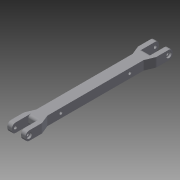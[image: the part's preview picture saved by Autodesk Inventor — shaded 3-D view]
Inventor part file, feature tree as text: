
AUTODESK INVENTOR PART (.ipt)
format: ipt  version: 2015 (Build 190159000, 159)  size: 180,736 bytes
history: native  units: mm
features: sketch x5, fillet x4, extrude x2, plane x2, hole x2, mirror x2, loft x1, other x1
ambient origin geometry x8: Origin, YZ Plane, XZ Plane, XY Plane, X Axis, Y Axis, Z Axis, Center Point
bodies: Solid1 (feature_tree)
feature tree (19):
  extrude  "Extrusion1"  Depth=10.0mm
  sketch  "Sketch2"  dims[d2=126.0mm d3=0.0mm d4=5.0mm]
  sketch  "Sketch3"  dims[d5=5.0mm d6=5.05mm d7=5.05mm d8=10.0mm]
  extrude  "Extrusion3"  Depth=5.0mm
  loft  "Loft2"
  plane  "Work Plane2"
  fillet  "Fillet4"  Radius=5.05mm
  fillet  "Fillet5"  Radius=10.0mm
  hole  "Hole1"  [1 undecoded]
  mirror  "Mirror2"
  plane  "Work Plane3"
  mirror  "Mirror3"
  hole  "Hole2"  [1 undecoded]
  fillet  "Fillet6"  Radius=4.0mm
  fillet  "Fillet7"  Radius=15.0mm
  sketch  "Sketch1"  dims[d0=12.0mm d1=10.0mm]
  other  "Edges1"
  sketch  "Sketch5"  dims[d18=18.0mm d19=0.0mm d20=0.0mm d21=90.0deg]
  sketch  "Sketch7"  dims[d22=0.0mm d23=90.0deg d24=4.0mm d25=4.0mm d26=3.3mm d27=6.0mm d28=6.0mm d29=2.0mm d30=90.0deg d31=8.0mm d32=20.594885mm d33=15.0mm d34=15.0mm d35=3.2mm d36=6.0mm d37=6.0mm d38=3.0mm d39=90.0deg d40=8.0mm d41=20.594885mm d42=3.0mm d43=3.0mm]
note: 2 required parameter values undecoded (feature->parameter linkage not recoverable at this tier; creation-order binding heuristic only, values carry confidence <= 0.55)
